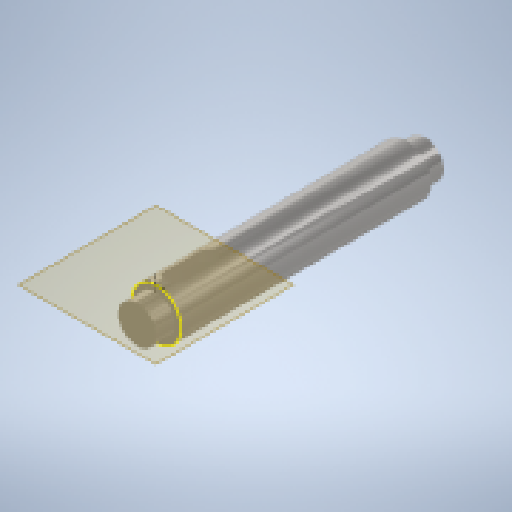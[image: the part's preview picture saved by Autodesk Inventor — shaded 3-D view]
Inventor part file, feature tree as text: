
AUTODESK INVENTOR PART (.ipt)
format: ipt  version: 2024 (Build 280153000, 153)  size: 173,056 bytes
history: native  units: mm
features: sketch x3, other x2, revolve x1, extrude x1
ambient origin geometry x8: Origin, YZ Plane, XZ Plane, XY Plane, X Axis, Y Axis, Z Axis, Center Point
bodies: Body1 (feature_tree)
feature tree (7):
  other  "ソリッド1"
  revolve  "回転1"
  sketch  "スケッチ2"
  other  "作業平面1"
  extrude  "押し出し1"  Depth=3.0mm
  sketch  "スケッチ1"
  sketch  "スケッチ3"
